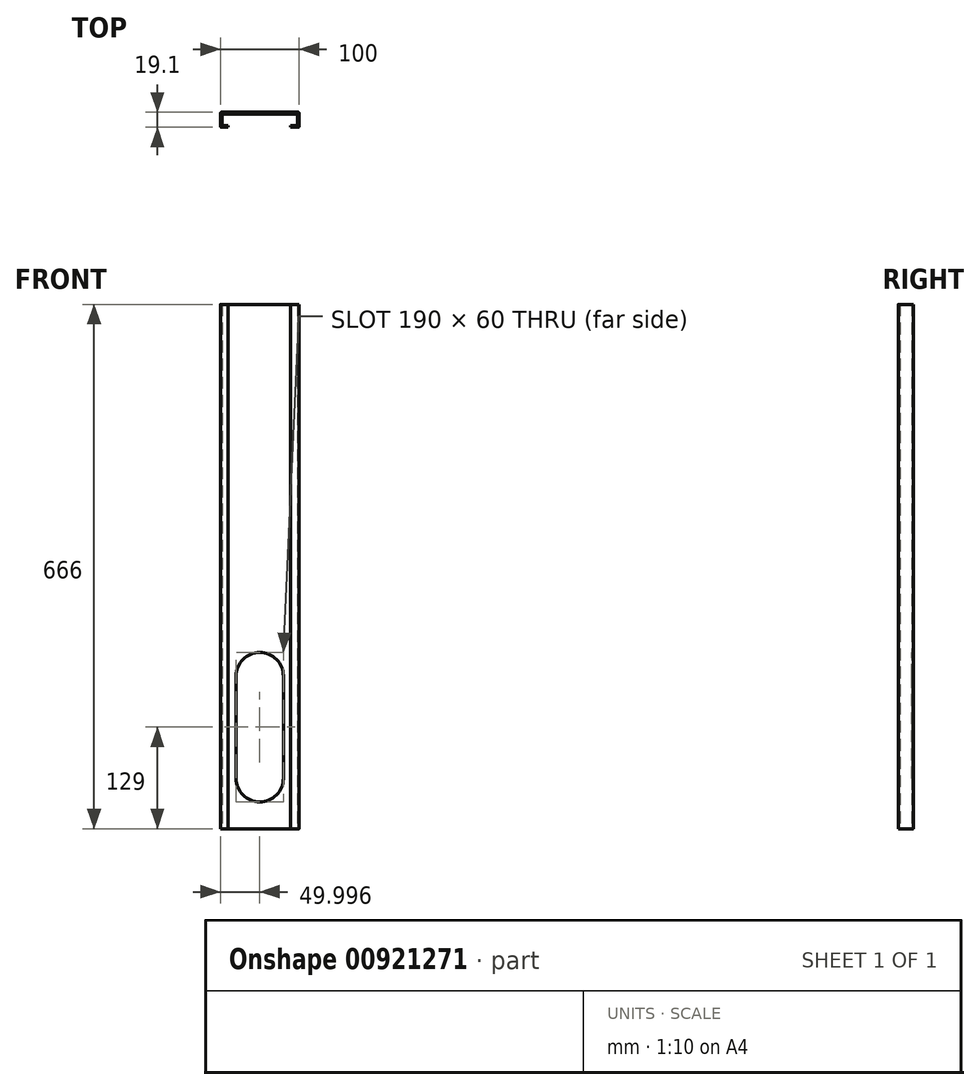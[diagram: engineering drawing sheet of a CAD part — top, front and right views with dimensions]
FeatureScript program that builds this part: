
annotation { "Feature Type Name" : "Feature", "Feature Type Description" : "" }
export const myFeature = defineFeature(function(context is Context, id is Id, definition is map)
    precondition{}
    {
        {
            var Q0;
            Q0=qCreatedBy(makeId("Top.planeOp"),FACE);
            var sketch = newSketch(context, id + "F0", { "sketchPlane" : qUnion([Q0])});
            skLineSegment(sketch, "E0", {"start": v(-51.84, 23.87) * mm, "end": v(46.16, 23.87) * mm});
            skLineSegment(sketch, "E1", {"start": v(-52.84, 22.87) * mm, "end": v(-52.84, 5.77) * mm});
            skLineSegment(sketch, "E2", {"start": v(47.16, 22.87) * mm, "end": v(47.16, 5.77) * mm});
            skLineSegment(sketch, "E3", {"start": v(-51.84, 4.77) * mm, "end": v(-42.84, 4.77) * mm});
            skLineSegment(sketch, "E4", {"start": v(-42.84, 4.77) * mm, "end": v(-42.84, 6.77) * mm});
            skLineSegment(sketch, "E5", {"start": v(-42.84, 6.77) * mm, "end": v(-49.84, 6.77) * mm});
            skLineSegment(sketch, "E6", {"start": v(-50.84, 7.77) * mm, "end": v(-50.84, 20.87) * mm});
            skLineSegment(sketch, "E7", {"start": v(-49.84, 21.87) * mm, "end": v(44.16, 21.87) * mm});
            skLineSegment(sketch, "E8", {"start": v(45.16, 20.87) * mm, "end": v(45.16, 7.77) * mm});
            skLineSegment(sketch, "E9", {"start": v(44.16, 6.77) * mm, "end": v(36.39, 6.77) * mm});
            skLineSegment(sketch, "E10", {"start": v(36.39, 6.77) * mm, "end": v(36.39, 4.77) * mm});
            skLineSegment(sketch, "E11", {"start": v(36.39, 4.77) * mm, "end": v(46.16, 4.77) * mm});
            skLineSegment(sketch, "E12", {"start": v(-52.84, 14.32) * mm, "end": v(-50.84, 14.32) * mm, "construction": true});
            skLineSegment(sketch, "E13", {"start": v(-2.84, 23.87) * mm, "end": v(-2.84, 21.87) * mm, "construction": true});
            skLineSegment(sketch, "E14", {"start": v(45.16, 14.32) * mm, "end": v(47.16, 14.32) * mm, "construction": true});
            skPoint(sketch, "E15.visualSharp", {"position": v(-50.84, 21.87) * mm});
            skArc(sketch, "E15.filletArc", {"start": v(-49.84, 21.87) * mm, "mid": v(-50.55, 21.58) * mm, "end": v(-50.84, 20.87) * mm});
            skPoint(sketch, "E16.visualSharp", {"position": v(-52.84, 23.87) * mm});
            skArc(sketch, "E16.filletArc", {"start": v(-51.84, 23.87) * mm, "mid": v(-52.55, 23.58) * mm, "end": v(-52.84, 22.87) * mm});
            skPoint(sketch, "E17.visualSharp", {"position": v(-52.84, 4.77) * mm});
            skArc(sketch, "E17.filletArc", {"start": v(-52.84, 5.77) * mm, "mid": v(-52.55, 5.07) * mm, "end": v(-51.84, 4.77) * mm});
            skPoint(sketch, "E18.visualSharp", {"position": v(-50.84, 6.77) * mm});
            skArc(sketch, "E18.filletArc", {"start": v(-50.84, 7.77) * mm, "mid": v(-50.55, 7.07) * mm, "end": v(-49.84, 6.77) * mm});
            skPoint(sketch, "E19.visualSharp", {"position": v(45.16, 21.87) * mm});
            skArc(sketch, "E19.filletArc", {"start": v(45.16, 20.87) * mm, "mid": v(44.86, 21.58) * mm, "end": v(44.16, 21.87) * mm});
            skPoint(sketch, "E20.visualSharp", {"position": v(47.16, 23.87) * mm});
            skArc(sketch, "E20.filletArc", {"start": v(47.16, 22.87) * mm, "mid": v(46.86, 23.58) * mm, "end": v(46.16, 23.87) * mm});
            skPoint(sketch, "E21.visualSharp", {"position": v(47.16, 4.77) * mm});
            skArc(sketch, "E21.filletArc", {"start": v(46.16, 4.77) * mm, "mid": v(46.86, 5.07) * mm, "end": v(47.16, 5.77) * mm});
            skPoint(sketch, "E22.visualSharp", {"position": v(45.16, 6.77) * mm});
            skArc(sketch, "E22.filletArc", {"start": v(44.16, 6.77) * mm, "mid": v(44.86, 7.07) * mm, "end": v(45.16, 7.77) * mm});
            skSolve(sketch);
        }
        {
            var Q0;
            Q0=makeQuery(id+"F0.imprint","IMPRINT",FACE,{"disambiguationData":[TD([[makeQuery(id+"F0.imprint","IMPRINT",EDGE,{"derivedFrom":sQuery(id+"F0.wireOp",EDGE,"E0")}),-1.0]])]});
            extrude(context, id + "F1", {"entities" : qUnion([Q0]), "depth" : 666 * mm, "offsetDistance" : 25 * mm});
        }
        {
            var Q0;
            Q0=makeQuery(id+"F1.opExtrude","SWEPT_FACE",FACE,{"disambiguationData":[OSD([sQuery(id+"F0.wireOp",EDGE,"E7")])]});
            var sketch = newSketch(context, id + "F2", { "sketchPlane" : qUnion([Q0])});
            skArc(sketch, "E23", {"start": v(27.16, 64) * mm, "mid": v(-2.84, 34) * mm, "end": v(-32.84, 64) * mm});
            skLineSegment(sketch, "E24", {"start": v(-49.84, 64) * mm, "end": v(44.16, 64) * mm, "construction": true});
            skLineSegment(sketch, "E25", {"start": v(27.16, 64) * mm, "end": v(27.16, 194) * mm});
            skLineSegment(sketch, "E26", {"start": v(-32.84, 64) * mm, "end": v(-32.84, 194) * mm});
            skArc(sketch, "E27", {"start": v(-32.84, 194) * mm, "mid": v(-2.84, 224) * mm, "end": v(27.16, 194) * mm});
            skLineSegment(sketch, "E28", {"start": v(-2.84, 34) * mm, "end": v(-2.84, 224) * mm, "construction": true});
            skLineSegment(sketch, "E29", {"start": v(-2.84, 34) * mm, "end": v(-2.84, 0) * mm, "construction": true});
            skSolve(sketch);
        }
        {
            var Q0;
            Q0 = qSketchRegion(id + "F2", true);
            extrude(context, id + "F3", {"entities" : qUnion([Q0]), "operationType" : NewBodyOperationType.REMOVE, "endBound" : BoundingType.UP_TO_NEXT, "oppositeDirection" : true, "depth" : 25 * mm, "offsetDistance" : 25 * mm});
        }
    });
